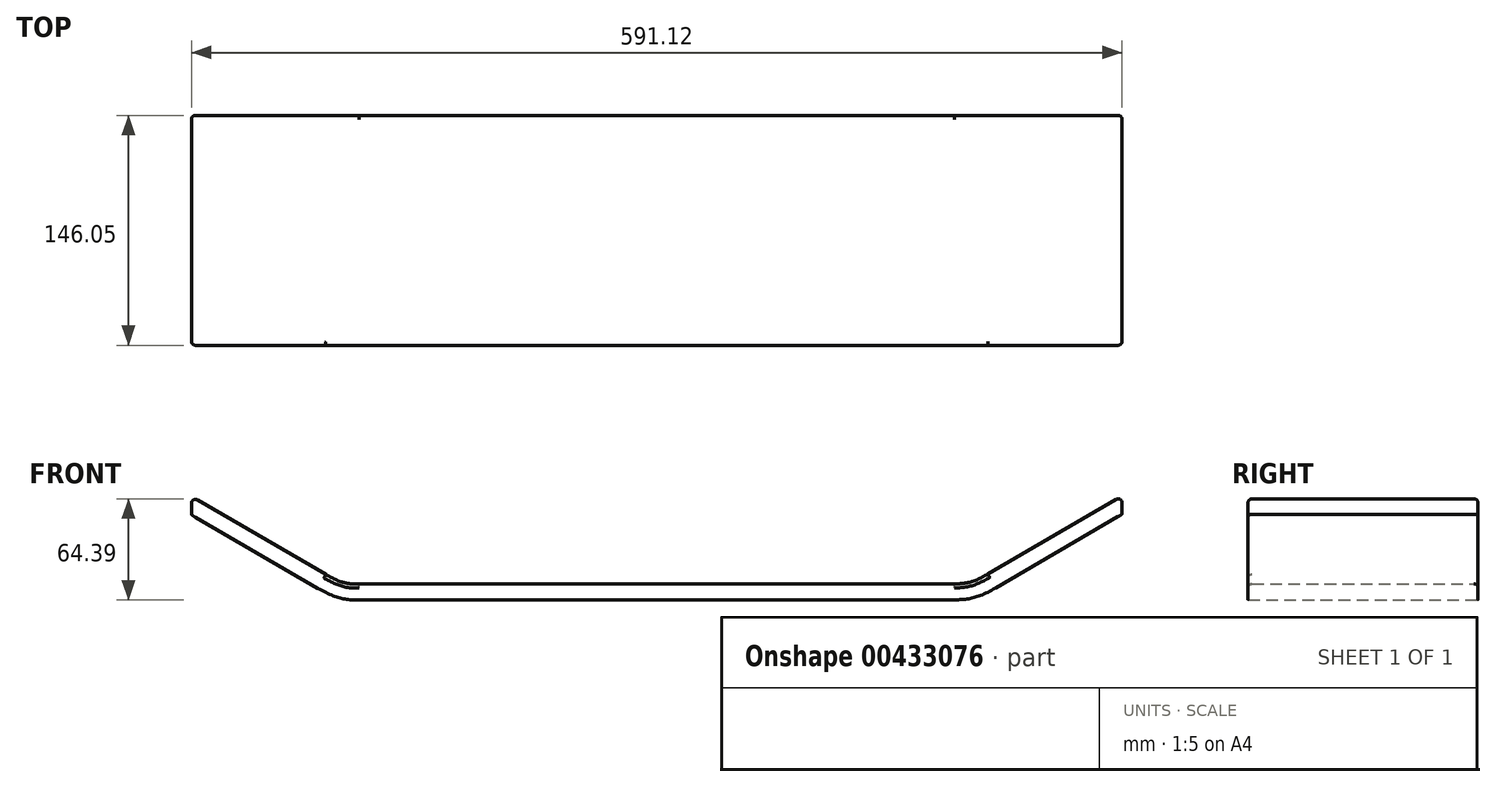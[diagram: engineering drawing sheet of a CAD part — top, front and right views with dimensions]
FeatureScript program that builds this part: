
annotation { "Feature Type Name" : "Feature", "Feature Type Description" : "" }
export const myFeature = defineFeature(function(context is Context, id is Id, definition is map)
    precondition{}
    {
        {
            var Q0;
            Q0=qCreatedBy(makeId("Front.planeOp"),FACE);
            var sketch = newSketch(context, id + "F0", { "sketchPlane" : qUnion([Q0])});
            skLineSegment(sketch, "E0", {"start": v(1.6, 54.16) * mm, "end": v(81.9, 7.54) * mm});
            skFitSpline(sketch, "E1", {"points": [v(81.9, 7.54) * mm, v(108.17, 0) * mm], "startDerivative": vector(31.2, -18.1) * mm, "endDerivative": vector(28.65, 0) * mm});
            skLineSegment(sketch, "E2", {"start": v(108.17, 0) * mm, "end": v(297.19, 0) * mm});
            skLineSegment(sketch, "E3.0", {"start": v(108.17, 10.16) * mm, "end": v(297.18, 10.16) * mm});
            skFitSpline(sketch, "E3.1", {"points": [v(87, 16.33) * mm, v(88.19, 15.64) * mm, v(90.4, 14.42) * mm, v(93.27, 13.02) * mm, v(95.8, 12) * mm, v(98.09, 11.26) * mm, v(100.3, 10.75) * mm, v(102.6, 10.4) * mm, v(105.15, 10.2) * mm, v(107.11, 10.16) * mm, v(108.17, 10.16) * mm]});
            skLineSegment(sketch, "E3.2", {"start": v(6.7, 62.94) * mm, "end": v(87, 16.33) * mm});
            skLineSegment(sketch, "E4", {"start": v(6.7, 62.94) * mm, "end": v(1.6, 65.9) * mm});
            skLineSegment(sketch, "E5", {"start": v(1.6, 65.9) * mm, "end": v(1.6, 54.16) * mm});
            skLineSegment(sketch, "E6", {"start": v(297.19, 0) * mm, "end": v(163.84, 0) * mm});
            skLineSegment(sketch, "E7.bottom", {"start": v(163.84, 0) * mm, "end": v(138.44, 0) * mm});
            skLineSegment(sketch, "E8", {"start": v(297.18, 10.16) * mm, "end": v(297.19, 0) * mm});
            skSolve(sketch);
        }
        {
            var Q0;
            Q0=makeQuery(id+"F0.imprint","IMPRINT",FACE,{"disambiguationData":[TD([[makeQuery(id+"F0.imprint","IMPRINT",EDGE,{"derivedFrom":sQuery(id+"F0.wireOp",EDGE,"E7.bottom")}),1.0]])]});
            var Q1;
            Q1=makeQuery(id+"F0.imprint","IMPRINT",FACE,{"disambiguationData":[TD([[makeQuery(id+"F0.imprint","IMPRINT",EDGE,{"derivedFrom":sQuery(id+"F0.wireOp",EDGE,"E0")}),1.0]])]});
            extrude(context, id + "F1", {"entities" : qUnion([Q0, Q1]), "depth" : 146.05 * mm});
        }
        {
            var Q0;
            Q0=makeQuery(id+"F1.opExtrude","CAP_EDGE",EDGE,{"disambiguationData":[OSD([sQuery(id+"F0.wireOp",EDGE,"E3.0")])],"isStart":true});
            var Q1;
            Q1=makeQuery(id+"F1.opExtrude","CAP_EDGE",EDGE,{"disambiguationData":[OSD([sQuery(id+"F0.wireOp",EDGE,"E3.1")])],"isStart":true});
            var Q2;
            Q2=makeQuery(id+"F1.opExtrude","CAP_EDGE",EDGE,{"disambiguationData":[OSD([sQuery(id+"F0.wireOp",EDGE,"E3.2"),sQuery(id+"F0.wireOp",EDGE,"E4")])],"isStart":true});
            var Q3;
            Q3=makeQuery(id+"F1.opExtrude","SWEPT_EDGE",EDGE,{"disambiguationData":[OSD([sQuery(id+"F0.wireOp",EDGE,"E4"),sQuery(id+"F0.wireOp",EDGE,"E5")])]});
            var Q4;
            Q4=makeQuery(id+"F1.opExtrude","CAP_EDGE",EDGE,{"disambiguationData":[OSD([sQuery(id+"F0.wireOp",EDGE,"E3.2"),sQuery(id+"F0.wireOp",EDGE,"E4")])],"isStart":false});
            var Q5;
            Q5=makeQuery(id+"F1.opExtrude","CAP_EDGE",EDGE,{"disambiguationData":[OSD([sQuery(id+"F0.wireOp",EDGE,"E3.1")])],"isStart":false});
            var Q6;
            Q6=makeQuery(id+"F1.opExtrude","CAP_EDGE",EDGE,{"disambiguationData":[OSD([sQuery(id+"F0.wireOp",EDGE,"E3.0")])],"isStart":false});
            var Q7;
            Q7=makeQuery(id+"F1.opExtrude","CAP_EDGE",EDGE,{"disambiguationData":[OSD([sQuery(id+"F0.wireOp",EDGE,"E5")])],"isStart":false});
            var Q8;
            Q8=makeQuery(id+"F1.opExtrude","CAP_EDGE",EDGE,{"disambiguationData":[OSD([sQuery(id+"F0.wireOp",EDGE,"E5")])],"isStart":true});
            fillet(context, id + "F2", {"entities" : qUnion([Q0, Q1, Q2, Q3, Q4, Q5, Q6, Q7, Q8]), "radius" : 2.54 * mm, "tangentPropagation" : true, "allowEdgeOverflow" : false});
        }
        {
            var Q0;
            Q0=makeQuery(id+"F1.opExtrude","SWEPT_BODY",BODY,{"disambiguationData":[OSD([sQuery(id+"F0.wireOp",EDGE,"E0"),sQuery(id+"F0.wireOp",EDGE,"E1"),sQuery(id+"F0.wireOp",EDGE,"E2"),sQuery(id+"F0.wireOp",EDGE,"E3.0"),sQuery(id+"F0.wireOp",EDGE,"E3.1"),sQuery(id+"F0.wireOp",EDGE,"E3.2"),sQuery(id+"F0.wireOp",EDGE,"E4"),sQuery(id+"F0.wireOp",EDGE,"E5"),sQuery(id+"F0.wireOp",EDGE,"E6"),sQuery(id+"F0.wireOp",EDGE,"E7.bottom"),sQuery(id+"F0.wireOp",EDGE,"E8")])]});
            var Q1;
            Q1=makeQuery(id+"F1.opExtrude","SWEPT_FACE",FACE,{"disambiguationData":[OSD([sQuery(id+"F0.wireOp",EDGE,"E8")])]});
            mirror(context, id + "F3", {"operationType" : NewBodyOperationType.ADD, "entities" : qUnion([Q0]), "mirrorPlane" : qUnion([Q1])});
        }
        {
            var Q0;
            Q0=makeQuery(id+"F1.opExtrude","SWEPT_BODY",BODY,{"disambiguationData":[OSD([sQuery(id+"F0.wireOp",EDGE,"E0"),sQuery(id+"F0.wireOp",EDGE,"E1"),sQuery(id+"F0.wireOp",EDGE,"E2"),sQuery(id+"F0.wireOp",EDGE,"E3.0"),sQuery(id+"F0.wireOp",EDGE,"E3.1"),sQuery(id+"F0.wireOp",EDGE,"E3.2"),sQuery(id+"F0.wireOp",EDGE,"E4"),sQuery(id+"F0.wireOp",EDGE,"E5"),sQuery(id+"F0.wireOp",EDGE,"E6"),sQuery(id+"F0.wireOp",EDGE,"E7.bottom"),sQuery(id+"F0.wireOp",EDGE,"E8")])]});
            transform(context, id + "F4", {"entities" : qUnion([Q0]), "transformType" : TransformType.TRANSLATION_3D, "dx" : 0 * mm, "dy" : 190.5 * mm, "dz" : 0 * mm, "makeCopy" : true});
        }
        {
            var Q0;
            Q0=makeQuery(id+"F4.opPattern","COPY",BODY,{"derivedFrom":makeQuery(id+"F1.opExtrude","SWEPT_BODY",BODY,{"disambiguationData":[OSD([sQuery(id+"F0.wireOp",EDGE,"E0"),sQuery(id+"F0.wireOp",EDGE,"E1"),sQuery(id+"F0.wireOp",EDGE,"E2"),sQuery(id+"F0.wireOp",EDGE,"E3.0"),sQuery(id+"F0.wireOp",EDGE,"E3.1"),sQuery(id+"F0.wireOp",EDGE,"E3.2"),sQuery(id+"F0.wireOp",EDGE,"E4"),sQuery(id+"F0.wireOp",EDGE,"E5"),sQuery(id+"F0.wireOp",EDGE,"E6"),sQuery(id+"F0.wireOp",EDGE,"E7.bottom"),sQuery(id+"F0.wireOp",EDGE,"E8")])]}),"instanceName":"1"});
            transform(context, id + "F5", {"entities" : qUnion([Q0]), "transformType" : TransformType.TRANSLATION_3D, "dx" : 0 * mm, "dy" : 190.5 * mm, "dz" : 0 * mm, "makeCopy" : true});
        }
        {
            var Q0;
            Q0=makeQuery(id+"F5.opPattern","COPY",BODY,{"derivedFrom":makeQuery(id+"F4.opPattern","COPY",BODY,{"derivedFrom":makeQuery(id+"F1.opExtrude","SWEPT_BODY",BODY,{"disambiguationData":[OSD([sQuery(id+"F0.wireOp",EDGE,"E0"),sQuery(id+"F0.wireOp",EDGE,"E1"),sQuery(id+"F0.wireOp",EDGE,"E2"),sQuery(id+"F0.wireOp",EDGE,"E3.0"),sQuery(id+"F0.wireOp",EDGE,"E3.1"),sQuery(id+"F0.wireOp",EDGE,"E3.2"),sQuery(id+"F0.wireOp",EDGE,"E4"),sQuery(id+"F0.wireOp",EDGE,"E5"),sQuery(id+"F0.wireOp",EDGE,"E6"),sQuery(id+"F0.wireOp",EDGE,"E7.bottom"),sQuery(id+"F0.wireOp",EDGE,"E8")])]}),"instanceName":"1"}),"instanceName":"1"});
            transform(context, id + "F6", {"entities" : qUnion([Q0]), "transformType" : TransformType.TRANSLATION_3D, "dx" : 0 * mm, "dy" : 190.5 * mm, "dz" : 0 * mm, "makeCopy" : true});
        }
        {
            var Q0;
            Q0=makeQuery(id+"F4.opPattern","COPY",BODY,{"derivedFrom":makeQuery(id+"F1.opExtrude","SWEPT_BODY",BODY,{"disambiguationData":[OSD([sQuery(id+"F0.wireOp",EDGE,"E0"),sQuery(id+"F0.wireOp",EDGE,"E1"),sQuery(id+"F0.wireOp",EDGE,"E2"),sQuery(id+"F0.wireOp",EDGE,"E3.0"),sQuery(id+"F0.wireOp",EDGE,"E3.1"),sQuery(id+"F0.wireOp",EDGE,"E3.2"),sQuery(id+"F0.wireOp",EDGE,"E4"),sQuery(id+"F0.wireOp",EDGE,"E5"),sQuery(id+"F0.wireOp",EDGE,"E6"),sQuery(id+"F0.wireOp",EDGE,"E7.bottom"),sQuery(id+"F0.wireOp",EDGE,"E8")])]}),"instanceName":"1"});
            var Q1;
            Q1=makeQuery(id+"F5.opPattern","COPY",BODY,{"derivedFrom":makeQuery(id+"F4.opPattern","COPY",BODY,{"derivedFrom":makeQuery(id+"F1.opExtrude","SWEPT_BODY",BODY,{"disambiguationData":[OSD([sQuery(id+"F0.wireOp",EDGE,"E0"),sQuery(id+"F0.wireOp",EDGE,"E1"),sQuery(id+"F0.wireOp",EDGE,"E2"),sQuery(id+"F0.wireOp",EDGE,"E3.0"),sQuery(id+"F0.wireOp",EDGE,"E3.1"),sQuery(id+"F0.wireOp",EDGE,"E3.2"),sQuery(id+"F0.wireOp",EDGE,"E4"),sQuery(id+"F0.wireOp",EDGE,"E5"),sQuery(id+"F0.wireOp",EDGE,"E6"),sQuery(id+"F0.wireOp",EDGE,"E7.bottom"),sQuery(id+"F0.wireOp",EDGE,"E8")])]}),"instanceName":"1"}),"instanceName":"1"});
            var Q2;
            Q2=makeQuery(id+"F6.opPattern","COPY",BODY,{"derivedFrom":makeQuery(id+"F5.opPattern","COPY",BODY,{"derivedFrom":makeQuery(id+"F4.opPattern","COPY",BODY,{"derivedFrom":makeQuery(id+"F1.opExtrude","SWEPT_BODY",BODY,{"disambiguationData":[OSD([sQuery(id+"F0.wireOp",EDGE,"E0"),sQuery(id+"F0.wireOp",EDGE,"E1"),sQuery(id+"F0.wireOp",EDGE,"E2"),sQuery(id+"F0.wireOp",EDGE,"E3.0"),sQuery(id+"F0.wireOp",EDGE,"E3.1"),sQuery(id+"F0.wireOp",EDGE,"E3.2"),sQuery(id+"F0.wireOp",EDGE,"E4"),sQuery(id+"F0.wireOp",EDGE,"E5"),sQuery(id+"F0.wireOp",EDGE,"E6"),sQuery(id+"F0.wireOp",EDGE,"E7.bottom"),sQuery(id+"F0.wireOp",EDGE,"E8")])]}),"instanceName":"1"}),"instanceName":"1"}),"instanceName":"1"});
            deleteBodies(context, id + "F7", {"entities" : qUnion([Q0, Q1, Q2])});
        }
    });
